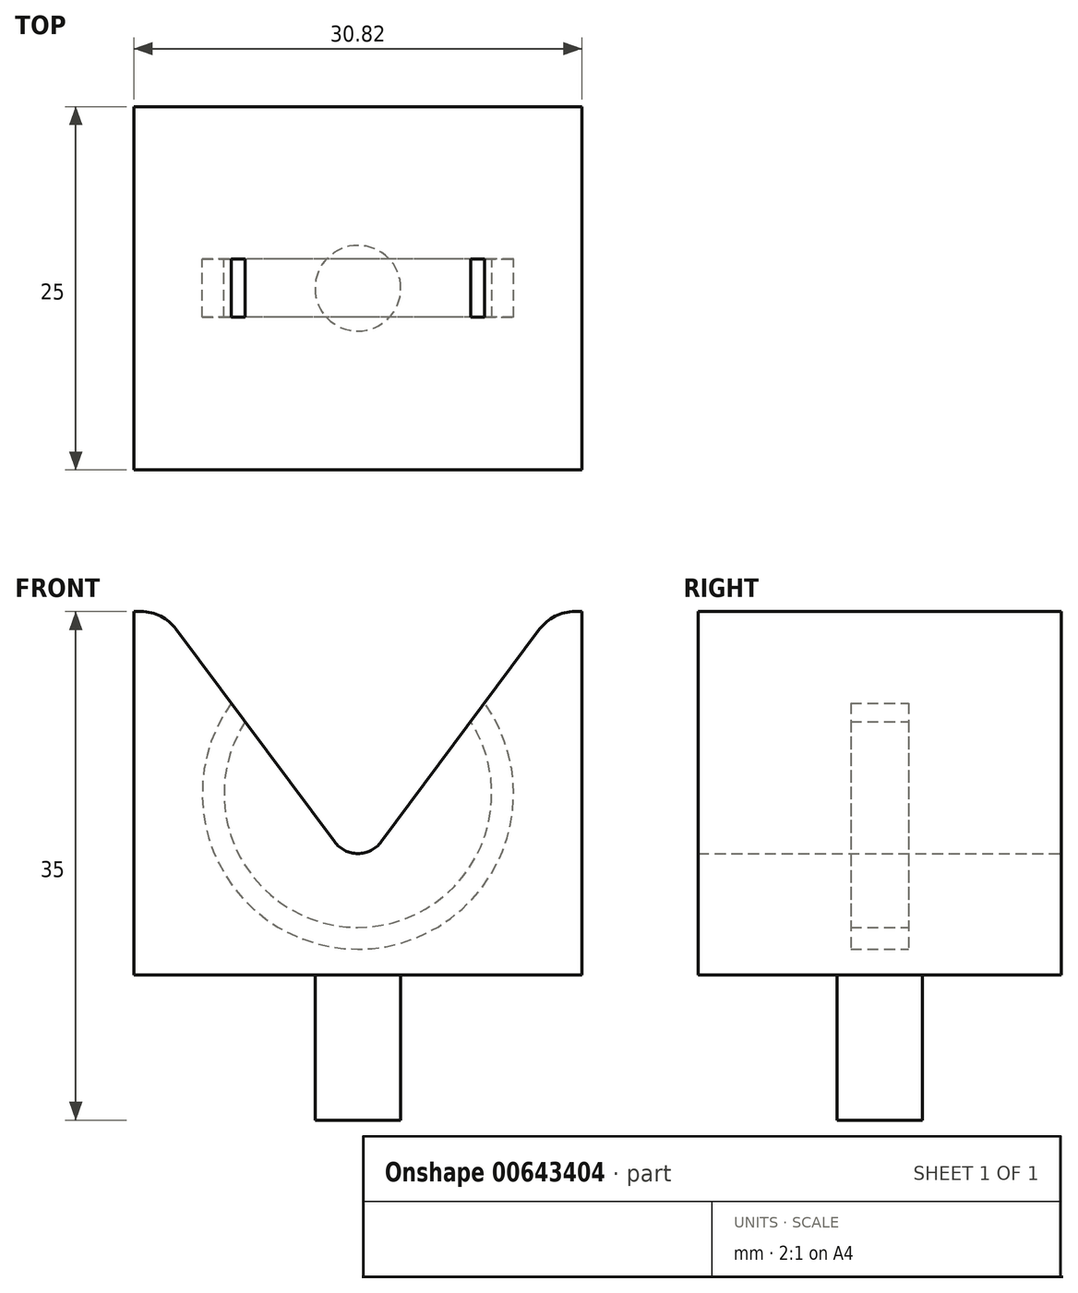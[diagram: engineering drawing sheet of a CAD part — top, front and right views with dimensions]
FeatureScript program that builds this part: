
annotation { "Feature Type Name" : "Feature", "Feature Type Description" : "" }
export const myFeature = defineFeature(function(context is Context, id is Id, definition is map)
    precondition{}
    {
        {
            var Q0;
            Q0=qCreatedBy(makeId("Front.planeOp"),FACE);
            var sketch = newSketch(context, id + "F0", { "sketchPlane" : qUnion([Q0])});
            skLineSegment(sketch, "E0", {"start": v(0, 0) * mm, "end": v(-15.4, 20.68) * mm});
            skLineSegment(sketch, "E1", {"start": v(-15.4, 20.68) * mm, "end": v(-15.4, -7) * mm});
            skLineSegment(sketch, "E2", {"start": v(-15.4, -7) * mm, "end": v(15.4, -7) * mm});
            skLineSegment(sketch, "E3", {"start": v(15.4, -7) * mm, "end": v(15.4, 20.68) * mm});
            skLineSegment(sketch, "E4", {"start": v(0, 0) * mm, "end": v(15.4, 20.68) * mm});
            skLineSegment(sketch, "E5", {"start": v(-15.4, 18) * mm, "end": v(-13.4, 18) * mm});
            skLineSegment(sketch, "E6", {"start": v(13.4, 18) * mm, "end": v(15.4, 18) * mm});
            skSolve(sketch);
        }
        {
            var Q0;
            {var subQ0=sQuery(id+"F0.wireOp",EDGE,"E2");Q0=makeQuery(id+"F0.imprint","IMPRINT",FACE,{"disambiguationData":[TD([[makeQuery(id+"F0.imprint","IMPRINT",EDGE,{"derivedFrom":subQ0}),1.0]])]});}
            extrude(context, id + "F1", {"entities" : qUnion([Q0]), "depth" : 25 * mm, "offsetDistance" : 25 * mm});
        }
        {
            var Q0;
            Q0=makeQuery(id+"F1.opExtrude","SWEPT_FACE",FACE,{"disambiguationData":[OSD([sQuery(id+"F0.wireOp",EDGE,"E2")])]});
            var sketch = newSketch(context, id + "F2", { "sketchPlane" : qUnion([Q0])});
            skPoint(sketch, "E7", {"position": v(0, 12.5) * mm});
            skPoint(sketch, "E7.positionSnap0", {"position": v(15.4, 12.5) * mm});
            skCircle(sketch, "E8", {"center": v(0, 12.5) * mm, "radius": 2.95 * mm});
            skSolve(sketch);
        }
        {
            var Q0;
            Q0=makeQuery(id+"F2.imprint","IMPRINT",FACE,{"disambiguationData":[TD([[makeQuery(id+"F2.imprint","IMPRINT",EDGE,{"derivedFrom":sQuery(id+"F2.wireOp",EDGE,"E8")}),1.0]])]});
            extrude(context, id + "F3", {"entities" : qUnion([Q0]), "operationType" : NewBodyOperationType.ADD, "depth" : 10 * mm, "offsetDistance" : 25 * mm});
        }
        {
            var Q0;
            Q0=makeQuery(id+"F1.opExtrude","SWEPT_EDGE",EDGE,{"disambiguationData":[OSD([sQuery(id+"F0.wireOp",EDGE,"E0"),sQuery(id+"F0.wireOp",EDGE,"E5")])]});
            var Q1;
            Q1=makeQuery(id+"F1.opExtrude","SWEPT_EDGE",EDGE,{"disambiguationData":[OSD([sQuery(id+"F0.wireOp",EDGE,"E4"),sQuery(id+"F0.wireOp",EDGE,"E6")])]});
            fillet(context, id + "F4", {"entities" : qUnion([Q0, Q1]), "radius" : 3 * mm, "tangentPropagation" : true, "allowEdgeOverflow" : false});
        }
        {
            var Q0;
            Q0=makeQuery(id+"F1.opExtrude","SWEPT_EDGE",EDGE,{"disambiguationData":[OSD([sQuery(id+"F0.wireOp",EDGE,"E0"),sQuery(id+"F0.wireOp",EDGE,"E4")])]});
            fillet(context, id + "F5", {"entities" : qUnion([Q0]), "radius" : 2 * mm, "tangentPropagation" : true, "allowEdgeOverflow" : false});
        }
        {
            var Q0;
            Q0=makeQuery(id+"F1.opExtrude","SWEPT_FACE",FACE,{"disambiguationData":[OSD([sQuery(id+"F0.wireOp",EDGE,"E2")])]});
            var sketch = newSketch(context, id + "F6", { "sketchPlane" : qUnion([Q0])});
            skLineSegment(sketch, "E9", {"start": v(-15.4, 12.5) * mm, "end": v(15.4, 12.5) * mm, "construction": true});
            skSolve(sketch);
        }
        {
            var Q0;
            Q0=sQuery(id+"F6.wireOp",EDGE,"E9");
            cPlane(context, id + "F7", {"entities" : qUnion([Q0]), "cplaneType" : CPlaneType.LINE_ANGLE, "offset" : 25 * mm, "angle" : 0 * degree, "width" : 150 * mm, "height" : 150 * mm});
        }
        {
            var Q0;
            Q0=qCreatedBy(id+"F7.planeOp",FACE);
            var sketch = newSketch(context, id + "F8", { "sketchPlane" : qUnion([Q0])});
            skPoint(sketch, "E10", {"position": v(-7.77, 10.43) * mm});
            skPoint(sketch, "E11", {"position": v(7.77, 10.43) * mm});
            skCircle(sketch, "E12", {"center": v(0, 5.48) * mm, "radius": 9.2 * mm});
            skCircle(sketch, "E13", {"center": v(0, 5.48) * mm, "radius": 10.7 * mm});
            skSolve(sketch);
        }
        {
            var Q0;
            Q0=makeQuery(id+"F8.imprint","IMPRINT",FACE,{"disambiguationData":[TD([[makeQuery(id+"F8.imprint","IMPRINT",EDGE,{"derivedFrom":sQuery(id+"F8.wireOp",EDGE,"E12")}),-1.0]])]});
            extrude(context, id + "F9", {"entities" : qUnion([Q0]), "operationType" : NewBodyOperationType.REMOVE, "endBound" : BoundingType.SYMMETRIC, "oppositeDirection" : true, "depth" : 4 * mm, "offsetDistance" : 25 * mm});
        }
    });
